# Revit family: A2LED
name_source: partatom
category: Lighting Fixtures
units: mm (PartAtom-declared; Revit-internal decimal feet)

## family parameters
Cut with Voids When Loaded = No
Host = Face
Light Source = Yes
OmniClass Number = 23.80.70.11.14.11
OmniClass Title = Downlights
Part Type = Normal
Room Calculation Point = No
Round Connector Dimension = Use Diameter
Shared = Yes

## types (1)
- A2LED
    Apparent Load = 0 VA
    Assembly Code = D5020200
    Back Plate = Black
    Color Filter = 16777215
    Default Elevation = 48.000"
    Description = The A2LED Series of specification grade LED adjustables are designed for use in a variety of architectural, retail, commercial and instituaitonal applications.
    Dimming Lamp Color Temperature Shift = <None>
    Emit Shape Visible in Rendering = No
    Emit from Circle Diameter = 2.500"
    Housing = Steel
    Input Power = 14 W
    Lamp = LED
    Load Classification = Lighting
    Manufacturer = Prescolite
    Model = A2LED
    Photometric Web File = AB2LED-2AB9LED7L30K8FL35.IES
    Power Factor = 1
    Reflector = Aluminum
    Tilt Angle = -90.00°
    URL = https://www.currentlighting.com
    Voltage = 120 V
    Wattage Comments = 13.8W to 22.4 W

## geometry (parser evidence)
native form markers: Blend x6, Sweep x2
no freeform markers — native parametric forms only
